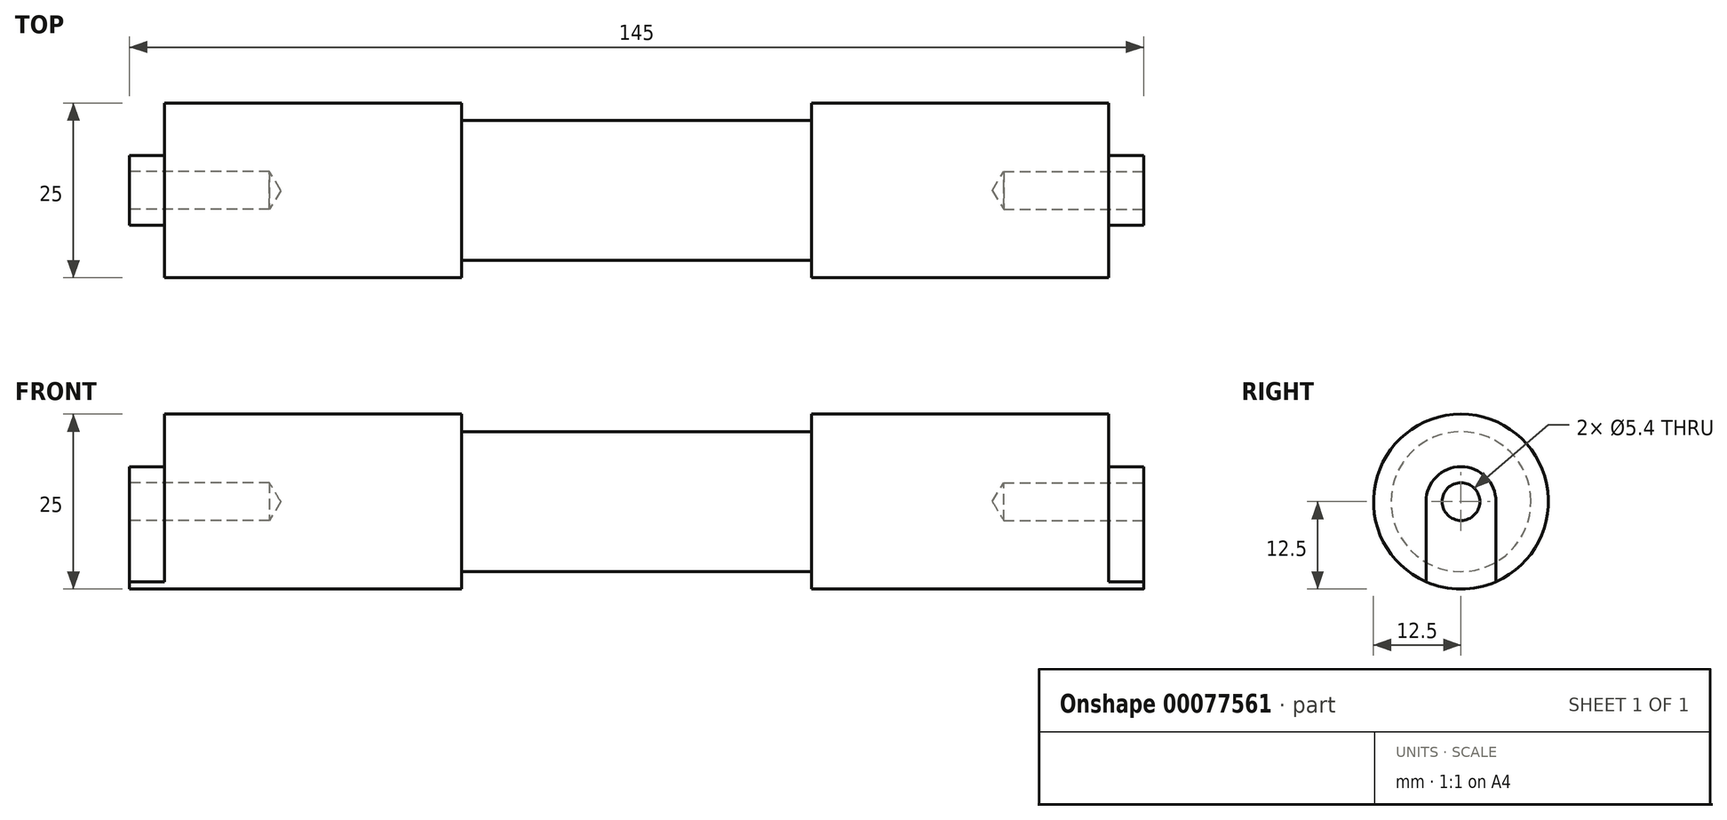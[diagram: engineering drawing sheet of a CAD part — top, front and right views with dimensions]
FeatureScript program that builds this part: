
annotation { "Feature Type Name" : "Feature", "Feature Type Description" : "" }
export const myFeature = defineFeature(function(context is Context, id is Id, definition is map)
    precondition{}
    {
        {
            var Q0;
            Q0=qCreatedBy(makeId("Right.planeOp"),FACE);
            var sketch = newSketch(context, id + "F0", { "sketchPlane" : qUnion([Q0])});
            skCircle(sketch, "E0", {"center": v(0, 0) * mm, "radius": 10 * mm});
            skSolve(sketch);
        }
        {
            var Q0;
            Q0 = qSketchRegion(id + "F0", true);
            extrude(context, id + "F1", {"entities" : qUnion([Q0]), "endBound" : BoundingType.SYMMETRIC, "depth" : 50 * mm});
        }
        {
            var Q0;
            Q0=makeQuery(id+"F1.opExtrude","CAP_FACE",FACE,{"disambiguationData":[OSD([sQuery(id+"F0.wireOp",EDGE,"E0")])],"isStart":false});
            var sketch = newSketch(context, id + "F2", { "sketchPlane" : qUnion([Q0])});
            skCircle(sketch, "E1", {"center": v(0, 0) * mm, "radius": 12.5 * mm});
            skSolve(sketch);
        }
        {
            var Q0;
            Q0 = qSketchRegion(id + "F2", true);
            extrude(context, id + "F3", {"entities" : qUnion([Q0]), "operationType" : NewBodyOperationType.ADD, "depth" : 42.5 * mm});
        }
        {
            var Q0;
            Q0=makeQuery(id+"F1.opExtrude","CAP_FACE",FACE,{"disambiguationData":[OSD([sQuery(id+"F0.wireOp",EDGE,"E0")])],"isStart":true});
            var sketch = newSketch(context, id + "F4", { "sketchPlane" : qUnion([Q0])});
            skCircle(sketch, "E2", {"center": v(0, 0) * mm, "radius": 12.5 * mm});
            skSolve(sketch);
        }
        {
            var Q0;
            Q0 = qSketchRegion(id + "F4", true);
            extrude(context, id + "F5", {"entities" : qUnion([Q0]), "operationType" : NewBodyOperationType.ADD, "depth" : 42.5 * mm});
        }
        {
            var Q0;
            Q0=makeQuery(id+"F3.opExtrude","CAP_FACE",FACE,{"disambiguationData":[OSD([sQuery(id+"F2.wireOp",EDGE,"E1")])],"isStart":false});
            var sketch = newSketch(context, id + "F6", { "sketchPlane" : qUnion([Q0])});
            skCircle(sketch, "E3", {"center": v(0, 0) * mm, "radius": 5 * mm});
            skLineSegment(sketch, "E4", {"start": v(5, 0) * mm, "end": v(5, -11.46) * mm});
            skLineSegment(sketch, "E5", {"start": v(-5, 0) * mm, "end": v(-5, -11.46) * mm});
            skSolve(sketch);
        }
        {
            var Q0;
            {var subQ0=sQuery(id+"F6.wireOp",EDGE,"E4");Q0=makeQuery(id+"F6.imprint","IMPRINT",FACE,{"disambiguationData":[TD([[makeQuery(id+"F6.imprint","IMPRINT",EDGE,{"derivedFrom":subQ0}),-1.0]])]});}
            var Q1;
            {var subQ0=sQuery(id+"F6.wireOp",EDGE,"E3");var subQ1=makeQuery(id+"F6.imprint","INTERSECT",VERTEX,{"derivedFrom":[subQ0,sQuery(id+"F6.wireOp",EDGE,"E4")]});Q1=makeQuery(id+"F6.imprint","IMPRINT",FACE,{"disambiguationData":[TD([[makeQuery(id+"F6.imprint","IMPRINT",EDGE,{"disambiguationData":[TD([[subQ1,-1.0]])],"derivedFrom":subQ0}),1.0]])]});}
            extrude(context, id + "F7", {"entities" : qUnion([Q0, Q1]), "operationType" : NewBodyOperationType.ADD, "depth" : 5 * mm});
        }
        {
            var Q0;
            Q0=makeQuery(id+"F7.opExtrude","CAP_FACE",FACE,{"disambiguationData":[OSD([sQuery(id+"F2.wireOp",EDGE,"E1"),sQuery(id+"F6.wireOp",EDGE,"E3"),sQuery(id+"F6.wireOp",EDGE,"E4"),sQuery(id+"F6.wireOp",EDGE,"E5")])],"isStart":false});
            var sketch = newSketch(context, id + "F8", { "sketchPlane" : qUnion([Q0])});
            skPoint(sketch, "E6", {"position": v(0, 0) * mm});
            skSolve(sketch);
        }
        {
            var Q0;
            Q0=sQuery(id+"F8.wireOp",VERTEX,"E6");
            var Q1;
            Q1=makeQuery(id+"F1.opExtrude","SWEPT_BODY",BODY,{"disambiguationData":[OSD([sQuery(id+"F0.wireOp",EDGE,"E0")])]});
            hole(context, id + "F9", {"style" : HoleStyle.SIMPLE, "endStyle" : HoleEndStyle.BLIND, "standardTappedOrClearance" : lookupTablePath({ "standard" : "ISO", "engagement" : "25%", "pitch" : "1 mm", "size" : "M6", "type" : "Tapped" }), "standardBlindInLast" : lookupTablePath({ "standard" : "ISO", "engagement" : "25%", "pitch" : "1 mm", "size" : "M6", "type" : "Tapped" }), "holeDiameter" : 5.4 * mm, "holeDepth" : 20 * mm, "startFromSketch" : true, "locations" : qUnion([Q0]), "scope" : qUnion([Q1])});
        }
        {
            var Q0;
            Q0=makeQuery(id+"F5.opExtrude","CAP_FACE",FACE,{"disambiguationData":[OSD([sQuery(id+"F4.wireOp",EDGE,"E2")])],"isStart":false});
            var sketch = newSketch(context, id + "F10", { "sketchPlane" : qUnion([Q0])});
            skCircle(sketch, "E7", {"center": v(0, 0) * mm, "radius": 5 * mm});
            skLineSegment(sketch, "E8", {"start": v(5, 0) * mm, "end": v(5, -11.46) * mm});
            skLineSegment(sketch, "E9", {"start": v(-5, 0) * mm, "end": v(-5, -11.46) * mm});
            skSolve(sketch);
        }
        {
            var Q0;
            {var subQ0=sQuery(id+"F10.wireOp",EDGE,"E7");var subQ1=makeQuery(id+"F10.imprint","INTERSECT",VERTEX,{"derivedFrom":[subQ0,sQuery(id+"F10.wireOp",EDGE,"E8")]});Q0=makeQuery(id+"F10.imprint","IMPRINT",FACE,{"disambiguationData":[TD([[makeQuery(id+"F10.imprint","IMPRINT",EDGE,{"disambiguationData":[TD([[subQ1,-1.0]])],"derivedFrom":subQ0}),1.0]])]});}
            var Q1;
            {var subQ0=sQuery(id+"F10.wireOp",EDGE,"E8");Q1=makeQuery(id+"F10.imprint","IMPRINT",FACE,{"disambiguationData":[TD([[makeQuery(id+"F10.imprint","IMPRINT",EDGE,{"derivedFrom":subQ0}),-1.0]])]});}
            extrude(context, id + "F11", {"entities" : qUnion([Q0, Q1]), "operationType" : NewBodyOperationType.ADD, "depth" : 5 * mm});
        }
        {
            var Q0;
            Q0=makeQuery(id+"F11.opExtrude","CAP_FACE",FACE,{"disambiguationData":[OSD([sQuery(id+"F4.wireOp",EDGE,"E2"),sQuery(id+"F10.wireOp",EDGE,"E7"),sQuery(id+"F10.wireOp",EDGE,"E8"),sQuery(id+"F10.wireOp",EDGE,"E9")])],"isStart":false});
            var sketch = newSketch(context, id + "F12", { "sketchPlane" : qUnion([Q0])});
            skPoint(sketch, "E10", {"position": v(0, 0) * mm});
            skSolve(sketch);
        }
        {
            var Q0;
            Q0=sQuery(id+"F12.wireOp",VERTEX,"E10");
            var Q1;
            Q1=makeQuery(id+"F1.opExtrude","SWEPT_BODY",BODY,{"disambiguationData":[OSD([sQuery(id+"F0.wireOp",EDGE,"E0")])]});
            hole(context, id + "F13", {"style" : HoleStyle.SIMPLE, "endStyle" : HoleEndStyle.BLIND, "standardTappedOrClearance" : lookupTablePath({ "standard" : "ISO", "engagement" : "25%", "pitch" : "1 mm", "size" : "M6", "type" : "Tapped" }), "standardBlindInLast" : lookupTablePath({ "standard" : "ISO", "engagement" : "25%", "pitch" : "1 mm", "size" : "M6", "type" : "Tapped" }), "holeDiameter" : 5.4 * mm, "holeDepth" : 20 * mm, "startFromSketch" : true, "locations" : qUnion([Q0]), "scope" : qUnion([Q1])});
        }
    });
